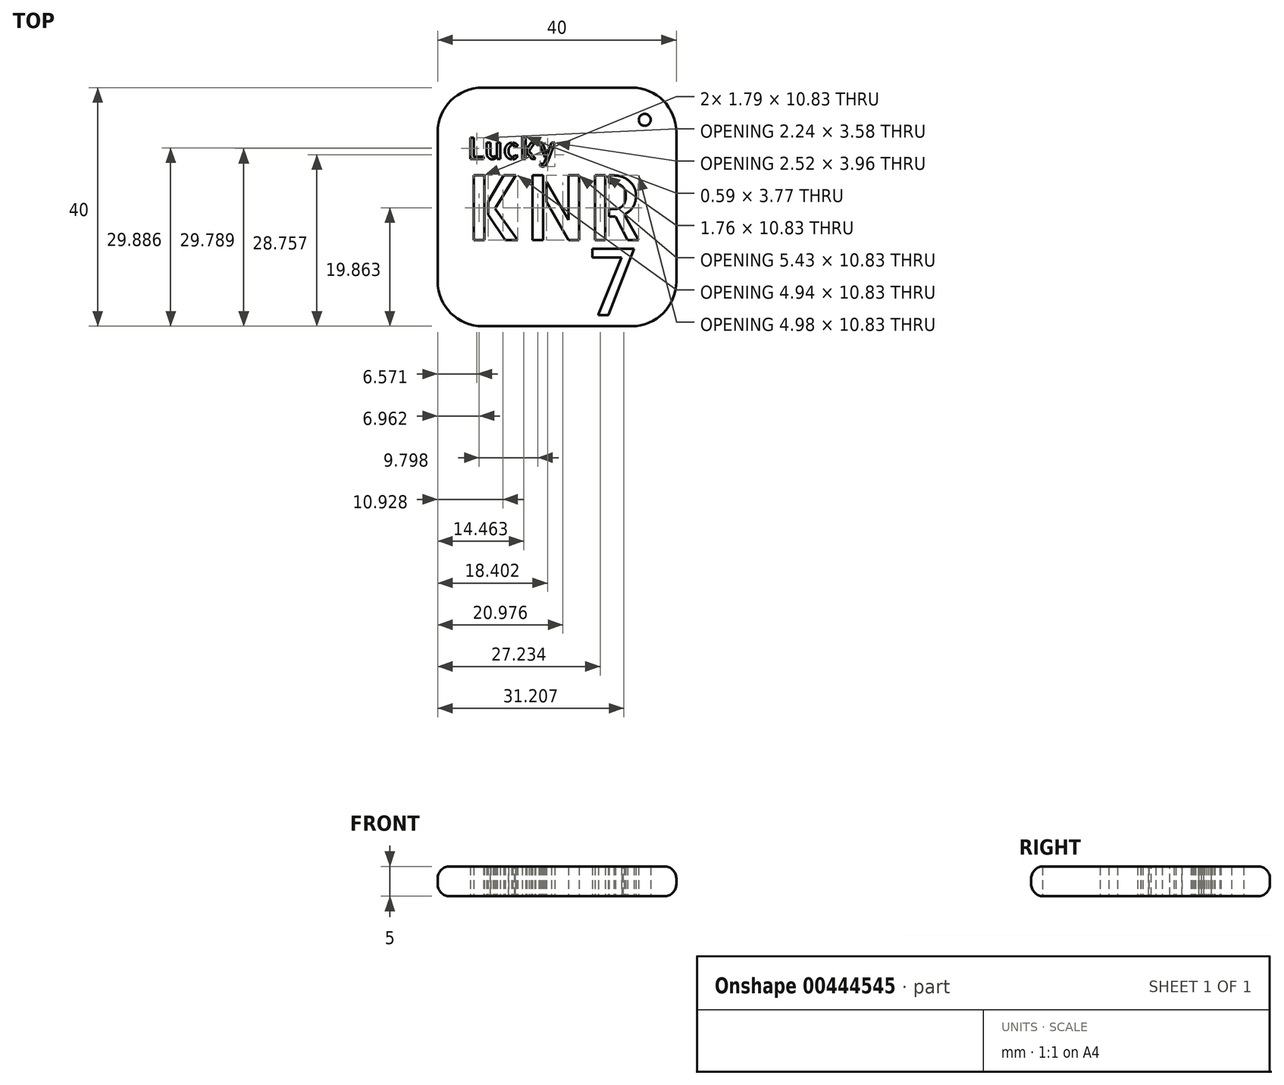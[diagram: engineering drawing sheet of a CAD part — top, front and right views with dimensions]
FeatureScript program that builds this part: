
annotation { "Feature Type Name" : "Feature", "Feature Type Description" : "" }
export const myFeature = defineFeature(function(context is Context, id is Id, definition is map)
    precondition{}
    {
        {
            var Q0;
            Q0=qCreatedBy(makeId("Top.planeOp"),FACE);
            var sketch = newSketch(context, id + "F0", { "sketchPlane" : qUnion([Q0])});
            skLineSegment(sketch, "E0.bottom", {"start": v(-12.5, 20) * mm, "end": v(12.5, 20) * mm});
            skLineSegment(sketch, "E0.top", {"start": v(-12.5, -20) * mm, "end": v(12.5, -20) * mm});
            skLineSegment(sketch, "E0.left", {"start": v(-20, 12.5) * mm, "end": v(-20, -12.5) * mm});
            skLineSegment(sketch, "E0.right", {"start": v(20, 12.5) * mm, "end": v(20, -12.5) * mm});
            skPoint(sketch, "E0.middle", {"position": v(0, 0) * mm});
            skPoint(sketch, "E1.visualSharp", {"position": v(-20, 20) * mm});
            skArc(sketch, "E1.filletArc", {"start": v(-12.5, 20) * mm, "mid": v(-17.8, 17.8) * mm, "end": v(-20, 12.5) * mm});
            skPoint(sketch, "E2.visualSharp", {"position": v(20, 20) * mm});
            skArc(sketch, "E2.filletArc", {"start": v(20, 12.5) * mm, "mid": v(17.8, 17.8) * mm, "end": v(12.5, 20) * mm});
            skPoint(sketch, "E3.visualSharp", {"position": v(-20, -20) * mm});
            skArc(sketch, "E3.filletArc", {"start": v(-20, -12.5) * mm, "mid": v(-17.8, -17.8) * mm, "end": v(-12.5, -20) * mm});
            skPoint(sketch, "E4.visualSharp", {"position": v(20, -20) * mm});
            skArc(sketch, "E4.filletArc", {"start": v(12.5, -20) * mm, "mid": v(17.8, -17.8) * mm, "end": v(20, -12.5) * mm});
            skSolve(sketch);
        }
        {
            var Q0;
            Q0 = qSketchRegion(id + "F0", true);
            extrude(context, id + "F1", {"entities" : qUnion([Q0]), "depth" : 5 * mm});
        }
        {
            var Q0;
            Q0=qCreatedBy(makeId("Top.planeOp"),FACE);
            var sketch = newSketch(context, id + "F2", { "sketchPlane" : qUnion([Q0])});
            skText(sketch, "E5", { "text": "KNR", "fontName": "AllertaStencil-Regular.ttf"});
            const initialGuessF2  = {"E5": [-0.0153, -0.00555, 1, 0, 0.01083]};
            skSetInitialGuess(sketch, initialGuessF2);
            skSolve(sketch);
        }
        {
            var Q0;
            Q0 = qSketchRegion(id + "F2", true);
            extrude(context, id + "F3", {"entities" : qUnion([Q0]), "operationType" : NewBodyOperationType.REMOVE, "depth" : 5 * mm});
        }
        {
            var Q0;
            Q0=qCreatedBy(makeId("Top.planeOp"),FACE);
            var sketch = newSketch(context, id + "F4", { "sketchPlane" : qUnion([Q0])});
            skText(sketch, "E6", { "text": "Lucky", "fontName": "AllertaStencil-Regular.ttf"});
            const initialGuessF4  = {"E6": [-0.015, 0.008, 1, 0, 0.00358]};
            skSetInitialGuess(sketch, initialGuessF4);
            skSolve(sketch);
        }
        {
            var Q0;
            Q0 = qSketchRegion(id + "F4", true);
            extrude(context, id + "F5", {"entities" : qUnion([Q0]), "operationType" : NewBodyOperationType.REMOVE, "depth" : 5 * mm});
        }
        {
            var Q0;
            Q0=qCreatedBy(makeId("Top.planeOp"),FACE);
            var sketch = newSketch(context, id + "F6", { "sketchPlane" : qUnion([Q0])});
            skText(sketch, "E7", { "text": "7", "fontName": "AllertaStencil-Regular.ttf"});
            const initialGuessF6  = {"E7": [0.005, -0.01811, 1, 0, 0.01111]};
            skSetInitialGuess(sketch, initialGuessF6);
            skSolve(sketch);
        }
        {
            var Q0;
            Q0 = qSketchRegion(id + "F6", true);
            extrude(context, id + "F7", {"entities" : qUnion([Q0]), "operationType" : NewBodyOperationType.REMOVE, "depth" : 25 * mm});
        }
        {
            var Q0;
            Q0=makeQuery(id+"F1.opExtrude","CAP_EDGE",EDGE,{"disambiguationData":[OSD([sQuery(id+"F0.wireOp",EDGE,"E2.filletArc")])],"isStart":false});
            fillet(context, id + "F8", {"entities" : qUnion([Q0]), "radius" : 2 * mm, "tangentPropagation" : true, "allowEdgeOverflow" : false});
        }
        {
            var Q0;
            Q0=makeQuery(id+"F1.opExtrude","CAP_EDGE",EDGE,{"disambiguationData":[OSD([sQuery(id+"F0.wireOp",EDGE,"E2.filletArc")])],"isStart":true});
            fillet(context, id + "F9", {"entities" : qUnion([Q0]), "radius" : 2 * mm, "tangentPropagation" : true, "allowEdgeOverflow" : false});
        }
        {
            var Q0;
            Q0=qCreatedBy(makeId("Top.planeOp"),FACE);
            var sketch = newSketch(context, id + "F10", { "sketchPlane" : qUnion([Q0])});
            skCircle(sketch, "E8", {"center": v(14.7, 14.58) * mm, "radius": 1 * mm});
            skSolve(sketch);
        }
        {
            var Q0;
            Q0=makeQuery(id+"F10.imprint","IMPRINT",FACE,{"disambiguationData":[TD([[makeQuery(id+"F10.imprint","IMPRINT",EDGE,{"derivedFrom":sQuery(id+"F10.wireOp",EDGE,"E8")}),1.0]])]});
            var Q1;
            Q1=sQuery(id+"F10.wireOp",EDGE,"E8");
            extrude(context, id + "F11", {"entities" : qUnion([Q0]), "operationType" : NewBodyOperationType.REMOVE, "surfaceEntities" : qUnion([Q1]), "depth" : 25 * mm});
        }
    });
